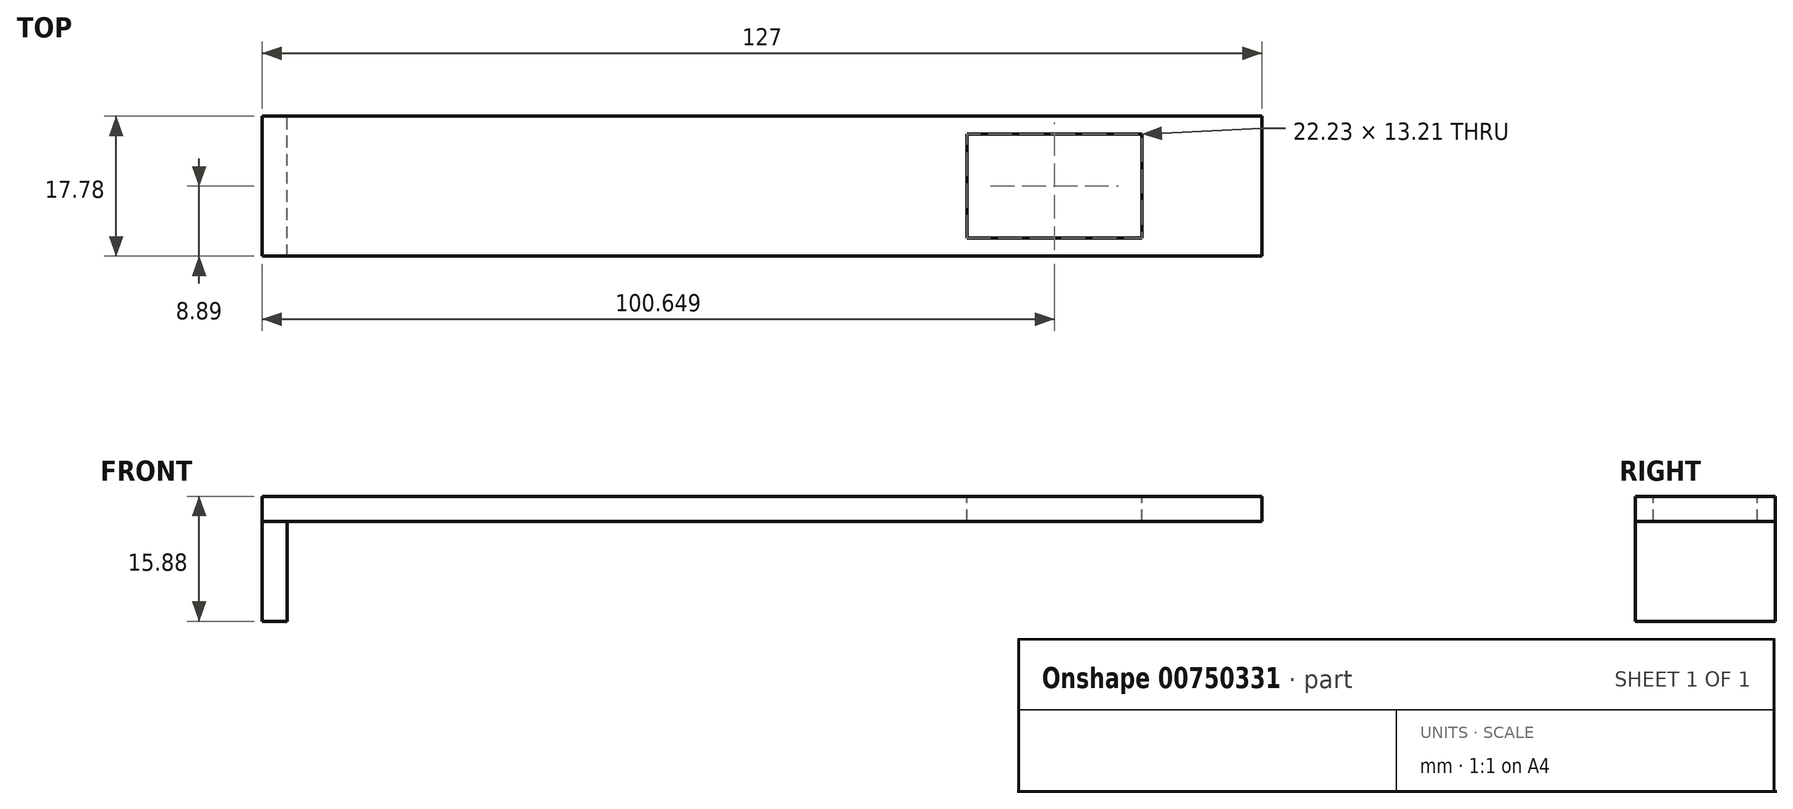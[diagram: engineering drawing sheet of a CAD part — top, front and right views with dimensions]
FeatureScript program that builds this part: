
annotation { "Feature Type Name" : "Feature", "Feature Type Description" : "" }
export const myFeature = defineFeature(function(context is Context, id is Id, definition is map)
    precondition{}
    {
        {
            var Q0;
            Q0=qCreatedBy(makeId("Front.planeOp"),FACE);
            var sketch = newSketch(context, id + "F0", { "sketchPlane" : qUnion([Q0])});
            skLineSegment(sketch, "E0.bottom", {"start": v(-64.17, -6.31) * mm, "end": v(62.83, -6.31) * mm});
            skLineSegment(sketch, "E0.top", {"start": v(-64.17, -9.49) * mm, "end": v(62.83, -9.49) * mm});
            skLineSegment(sketch, "E0.left", {"start": v(-64.17, -6.31) * mm, "end": v(-64.17, -9.49) * mm});
            skLineSegment(sketch, "E0.right", {"start": v(62.83, -6.31) * mm, "end": v(62.83, -9.49) * mm});
            skSolve(sketch);
        }
        {
            var Q0;
            Q0 = qSketchRegion(id + "F0", true);
            extrude(context, id + "F1", {"entities" : qUnion([Q0]), "depth" : 17.78 * mm, "offsetDistance" : 25.4 * mm});
        }
        {
            var Q0;
            Q0=makeQuery(id+"F1.opExtrude","SWEPT_FACE",FACE,{"disambiguationData":[OSD([sQuery(id+"F0.wireOp",EDGE,"E0.bottom")])]});
            var sketch = newSketch(context, id + "F2", { "sketchPlane" : qUnion([Q0])});
            skLineSegment(sketch, "E1.bottom", {"start": v(25.37, -2.29) * mm, "end": v(47.6, -2.29) * mm});
            skLineSegment(sketch, "E1.top", {"start": v(25.37, -15.5) * mm, "end": v(47.6, -15.5) * mm});
            skLineSegment(sketch, "E1.left", {"start": v(25.37, -2.29) * mm, "end": v(25.37, -15.5) * mm});
            skLineSegment(sketch, "E1.right", {"start": v(47.6, -2.29) * mm, "end": v(47.6, -15.5) * mm});
            skSolve(sketch);
        }
        {
            var Q0;
            Q0 = qSketchRegion(id + "F2", true);
            extrude(context, id + "F3", {"entities" : qUnion([Q0]), "operationType" : NewBodyOperationType.REMOVE, "oppositeDirection" : true, "depth" : 25.4 * mm, "offsetDistance" : 25.4 * mm});
        }
        {
            var Q0;
            Q0=makeQuery(id+"F1.opExtrude","SWEPT_FACE",FACE,{"disambiguationData":[OSD([sQuery(id+"F0.wireOp",EDGE,"E0.top")])]});
            var sketch = newSketch(context, id + "F4", { "sketchPlane" : qUnion([Q0])});
            skLineSegment(sketch, "E2.bottom", {"start": v(-64.17, 17.78) * mm, "end": v(-61, 17.78) * mm});
            skLineSegment(sketch, "E2.top", {"start": v(-64.17, 0) * mm, "end": v(-61, 0) * mm});
            skLineSegment(sketch, "E2.left", {"start": v(-64.17, 17.78) * mm, "end": v(-64.17, 0) * mm});
            skLineSegment(sketch, "E2.right", {"start": v(-61, 17.78) * mm, "end": v(-61, 0) * mm});
            skSolve(sketch);
        }
        {
            var Q0;
            Q0 = qSketchRegion(id + "F4", true);
            extrude(context, id + "F5", {"entities" : qUnion([Q0]), "depth" : 12.7 * mm, "offsetDistance" : 25.4 * mm});
        }
    });
